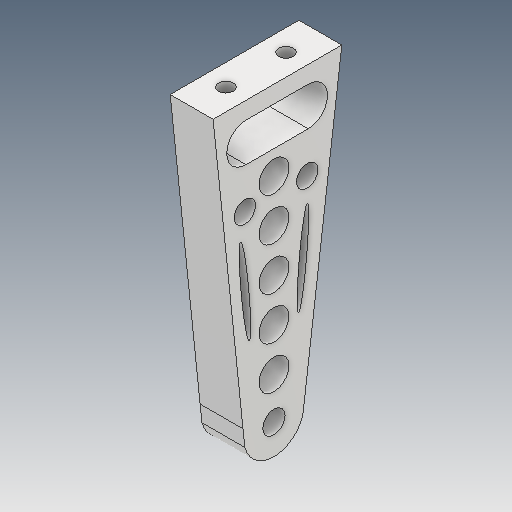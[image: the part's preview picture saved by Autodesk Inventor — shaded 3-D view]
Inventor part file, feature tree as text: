
AUTODESK INVENTOR PART (.ipt)
format: ipt  version: 2018 (Build 220112000, 112)  size: 212,480 bytes
history: native  units: mm
features: extrude x2, chamfer x2, sketch x2
ambient origin geometry x8: Origin, YZ Plane, XZ Plane, XY Plane, X Axis, Y Axis, Z Axis, Center Point
bodies: Volumenkörper1 (feature_tree)
feature tree (6):
  extrude  "Extrusion1"  Depth=10.0mm TaperAngle=0.0deg
  extrude  "Extrusion2"  Depth=3.4mm
  chamfer  "Fase1"  Distance=8.0mm
  chamfer  "Fase3"  Distance=3.4mm
  sketch  "Skizze1"  dims[d0=30.0mm d7=10.0mm d8=0.0mm]
  sketch  "Skizze3"  dims[d13=2.5mm d14=2.5mm d16=2.5mm d17=2.5mm d24=3.4mm d25=8.0mm d26=3.4mm d27=8.0mm d28=5.0mm d30=11.0mm d31=0.0mm d32=70.0mm d34=5.2mm d35=14.0mm d36=7.0mm d42=9.0mm d43=8.5mm d44=6.5mm d45=50.0mm d47=10.0mm d48=10.0mm d50=10.0mm d54=5.0mm d59=5.0mm d60=5.0mm d61=2.0mm d62=2.0mm d63=45.0deg d67=9.0mm d68=8.0mm d69=2.0mm d70=2.0mm d71=45.0deg]
